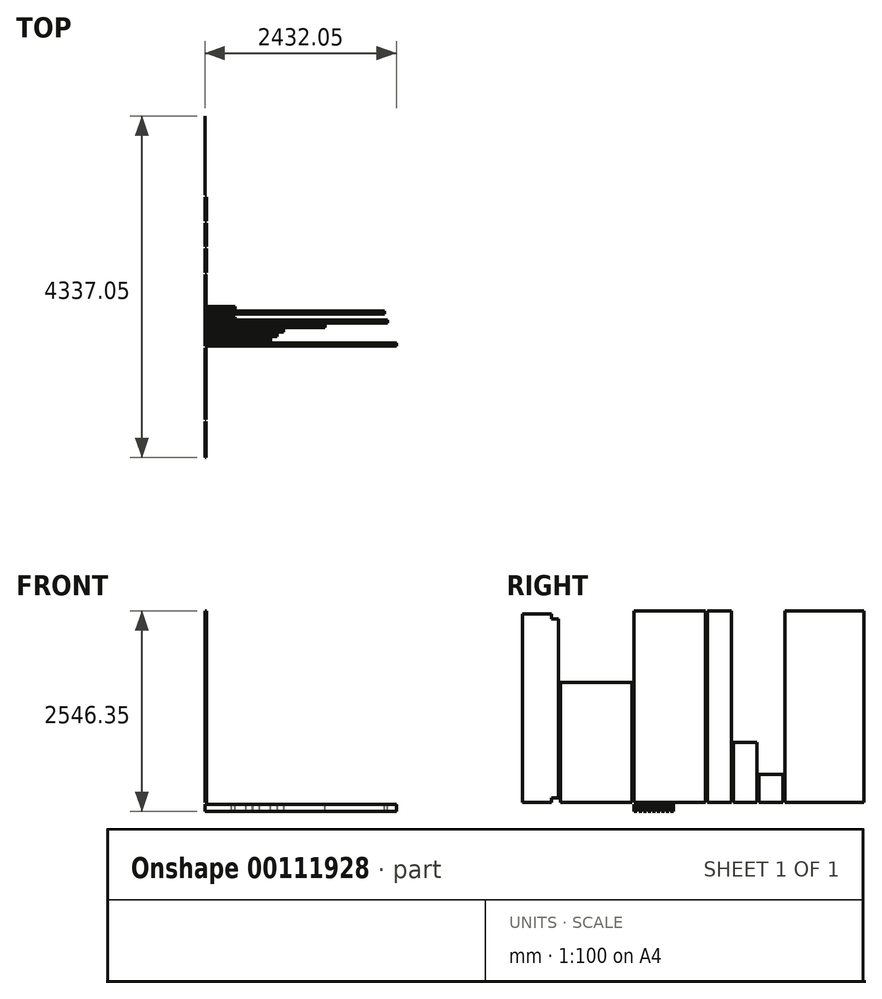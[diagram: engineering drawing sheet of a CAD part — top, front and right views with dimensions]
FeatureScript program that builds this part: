
annotation { "Feature Type Name" : "Feature", "Feature Type Description" : "" }
export const myFeature = defineFeature(function(context is Context, id is Id, definition is map)
    precondition{}
    {
        {
            var Q0;
            Q0=qCreatedBy(makeId("Right.planeOp"),FACE);
            var sketch = newSketch(context, id + "F0", { "sketchPlane" : qUnion([Q0])});
            skLineSegment(sketch, "E0.bottom", {"start": v(0, 0) * mm, "end": v(38.1, 0) * mm});
            skLineSegment(sketch, "E0.top", {"start": v(0, 88.9) * mm, "end": v(38.1, 88.9) * mm});
            skLineSegment(sketch, "E0.left", {"start": v(0, 0) * mm, "end": v(0, 88.9) * mm});
            skLineSegment(sketch, "E0.right", {"start": v(38.1, 0) * mm, "end": v(38.1, 88.9) * mm});
            skSolve(sketch);
        }
        {
            var Q0;
            Q0 = qSketchRegion(id + "F0", true);
            extrude(context, id + "F1", {"entities" : qUnion([Q0]), "depth" : 2432.05 * mm});
        }
        {
            var Q0;
            Q0=qCreatedBy(makeId("Right.planeOp"),FACE);
            var sketch = newSketch(context, id + "F2", { "sketchPlane" : qUnion([Q0])});
            skLineSegment(sketch, "E1.bottom", {"start": v(63.5, 0) * mm, "end": v(101.6, 0) * mm});
            skLineSegment(sketch, "E1.top", {"start": v(63.5, 88.9) * mm, "end": v(101.6, 88.9) * mm});
            skLineSegment(sketch, "E1.left", {"start": v(63.5, 0) * mm, "end": v(63.5, 88.9) * mm});
            skLineSegment(sketch, "E1.right", {"start": v(101.6, 0) * mm, "end": v(101.6, 88.9) * mm});
            skSolve(sketch);
        }
        {
            var Q0;
            Q0 = qSketchRegion(id + "F2", true);
            extrude(context, id + "F3", {"entities" : qUnion([Q0]), "depth" : 831.85 * mm});
        }
        {
            var Q0;
            Q0=qCreatedBy(makeId("Right.planeOp"),FACE);
            var sketch = newSketch(context, id + "F4", { "sketchPlane" : qUnion([Q0])});
            skLineSegment(sketch, "E2.bottom", {"start": v(120.65, 88.9) * mm, "end": v(158.75, 88.9) * mm});
            skLineSegment(sketch, "E2.top", {"start": v(120.65, 0) * mm, "end": v(158.75, 0) * mm});
            skLineSegment(sketch, "E2.left", {"start": v(120.65, 88.9) * mm, "end": v(120.65, 0) * mm});
            skLineSegment(sketch, "E2.right", {"start": v(158.75, 88.9) * mm, "end": v(158.75, 0) * mm});
            skLineSegment(sketch, "E3.bottom", {"start": v(177.8, 88.9) * mm, "end": v(215.9, 88.9) * mm});
            skLineSegment(sketch, "E3.top", {"start": v(177.8, 0) * mm, "end": v(215.9, 0) * mm});
            skLineSegment(sketch, "E3.left", {"start": v(177.8, 88.9) * mm, "end": v(177.8, 0) * mm});
            skLineSegment(sketch, "E3.right", {"start": v(215.9, 88.9) * mm, "end": v(215.9, 0) * mm});
            skLineSegment(sketch, "E4.bottom", {"start": v(0, 114.3) * mm, "end": v(908.05, 114.3) * mm});
            skLineSegment(sketch, "E4.top", {"start": v(0, 2546.35) * mm, "end": v(908.05, 2546.35) * mm});
            skLineSegment(sketch, "E4.left", {"start": v(0, 114.3) * mm, "end": v(0, 2546.35) * mm});
            skLineSegment(sketch, "E4.right", {"start": v(908.05, 114.3) * mm, "end": v(908.05, 2546.35) * mm});
            skLineSegment(sketch, "E5.bottom", {"start": v(933.45, 2546.35) * mm, "end": v(1238.25, 2546.35) * mm});
            skLineSegment(sketch, "E5.top", {"start": v(933.45, 114.3) * mm, "end": v(1238.25, 114.3) * mm});
            skLineSegment(sketch, "E5.left", {"start": v(933.45, 2546.35) * mm, "end": v(933.45, 114.3) * mm});
            skLineSegment(sketch, "E5.right", {"start": v(1238.25, 2546.35) * mm, "end": v(1238.25, 114.3) * mm});
            skLineSegment(sketch, "E6.bottom", {"start": v(1263.65, 876.3) * mm, "end": v(1562.1, 876.3) * mm});
            skLineSegment(sketch, "E6.top", {"start": v(1263.65, 114.3) * mm, "end": v(1562.1, 114.3) * mm});
            skLineSegment(sketch, "E6.left", {"start": v(1263.65, 876.3) * mm, "end": v(1263.65, 114.3) * mm});
            skLineSegment(sketch, "E6.right", {"start": v(1562.1, 876.3) * mm, "end": v(1562.1, 114.3) * mm});
            skLineSegment(sketch, "E7.bottom", {"start": v(1587.5, 114.3) * mm, "end": v(1892.3, 114.3) * mm});
            skLineSegment(sketch, "E7.top", {"start": v(1587.5, 469.9) * mm, "end": v(1892.3, 469.9) * mm});
            skLineSegment(sketch, "E7.left", {"start": v(1587.5, 114.3) * mm, "end": v(1587.5, 469.9) * mm});
            skLineSegment(sketch, "E7.right", {"start": v(1892.3, 114.3) * mm, "end": v(1892.3, 469.9) * mm});
            skLineSegment(sketch, "E8.bottom", {"start": v(234.95, 0) * mm, "end": v(273.05, 0) * mm});
            skLineSegment(sketch, "E8.top", {"start": v(234.95, 88.9) * mm, "end": v(273.05, 88.9) * mm});
            skLineSegment(sketch, "E8.left", {"start": v(234.95, 0) * mm, "end": v(234.95, 88.9) * mm});
            skLineSegment(sketch, "E8.right", {"start": v(273.05, 0) * mm, "end": v(273.05, 88.9) * mm});
            skLineSegment(sketch, "E9.bottom", {"start": v(-25.4, 114.3) * mm, "end": v(-933.45, 114.3) * mm});
            skLineSegment(sketch, "E9.top", {"start": v(-25.4, 1638.3) * mm, "end": v(-933.45, 1638.3) * mm});
            skLineSegment(sketch, "E9.left", {"start": v(-25.4, 114.3) * mm, "end": v(-25.4, 1638.3) * mm});
            skLineSegment(sketch, "E9.right", {"start": v(-933.45, 114.3) * mm, "end": v(-933.45, 1638.3) * mm});
            skLineSegment(sketch, "E10.bottom", {"start": v(292.1, 0) * mm, "end": v(330.2, 0) * mm});
            skLineSegment(sketch, "E10.top", {"start": v(292.1, 88.9) * mm, "end": v(330.2, 88.9) * mm});
            skLineSegment(sketch, "E10.left", {"start": v(292.1, 0) * mm, "end": v(292.1, 88.9) * mm});
            skLineSegment(sketch, "E10.right", {"start": v(330.2, 0) * mm, "end": v(330.2, 88.9) * mm});
            skLineSegment(sketch, "E11.bottom", {"start": v(349.25, 0) * mm, "end": v(387.35, 0) * mm});
            skLineSegment(sketch, "E11.top", {"start": v(349.25, 88.9) * mm, "end": v(387.35, 88.9) * mm});
            skLineSegment(sketch, "E11.left", {"start": v(349.25, 0) * mm, "end": v(349.25, 88.9) * mm});
            skLineSegment(sketch, "E11.right", {"start": v(387.35, 0) * mm, "end": v(387.35, 88.9) * mm});
            skLineSegment(sketch, "E12.bottom", {"start": v(406.4, 0) * mm, "end": v(444.5, 0) * mm});
            skLineSegment(sketch, "E12.top", {"start": v(406.4, 88.9) * mm, "end": v(444.5, 88.9) * mm});
            skLineSegment(sketch, "E12.left", {"start": v(406.4, 0) * mm, "end": v(406.4, 88.9) * mm});
            skLineSegment(sketch, "E12.right", {"start": v(444.5, 0) * mm, "end": v(444.5, 88.9) * mm});
            skLineSegment(sketch, "E13.bottom", {"start": v(463.55, 0) * mm, "end": v(501.65, 0) * mm});
            skLineSegment(sketch, "E13.top", {"start": v(463.55, 88.9) * mm, "end": v(501.65, 88.9) * mm});
            skLineSegment(sketch, "E13.left", {"start": v(463.55, 0) * mm, "end": v(463.55, 88.9) * mm});
            skLineSegment(sketch, "E13.right", {"start": v(501.65, 0) * mm, "end": v(501.65, 88.9) * mm});
            skLineSegment(sketch, "E14.bottom", {"start": v(-1047.75, 114.3) * mm, "end": v(-1416.05, 114.3) * mm});
            skLineSegment(sketch, "E14.top", {"start": v(-1047.75, 2508.25) * mm, "end": v(-1416.05, 2508.25) * mm});
            skLineSegment(sketch, "E14.left", {"start": v(-958.85, 174.63) * mm, "end": v(-958.85, 2447.93) * mm});
            skLineSegment(sketch, "E14.right", {"start": v(-1416.05, 114.3) * mm, "end": v(-1416.05, 2508.25) * mm});
            skLineSegment(sketch, "E15", {"start": v(-1047.75, 114.3) * mm, "end": v(-1047.75, 174.62) * mm});
            skLineSegment(sketch, "E16", {"start": v(-1047.75, 174.63) * mm, "end": v(-958.85, 174.63) * mm});
            skLineSegment(sketch, "E17", {"start": v(-1047.75, 2508.25) * mm, "end": v(-1047.75, 2447.93) * mm});
            skLineSegment(sketch, "E18", {"start": v(-1047.75, 2447.93) * mm, "end": v(-958.85, 2447.93) * mm});
            skLineSegment(sketch, "E19.bottom", {"start": v(1917.7, 114.3) * mm, "end": v(2921, 114.3) * mm});
            skLineSegment(sketch, "E19.top", {"start": v(1917.7, 2546.35) * mm, "end": v(2921, 2546.35) * mm});
            skLineSegment(sketch, "E19.left", {"start": v(1917.7, 114.3) * mm, "end": v(1917.7, 2546.35) * mm});
            skLineSegment(sketch, "E19.right", {"start": v(2921, 114.3) * mm, "end": v(2921, 2546.35) * mm});
            skSolve(sketch);
        }
        {
            var Q0;
            Q0=makeQuery(id+"F4.imprint","IMPRINT",FACE,{"disambiguationData":[TD([[makeQuery(id+"F4.imprint","IMPRINT",EDGE,{"derivedFrom":sQuery(id+"F4.wireOp",EDGE,"E2.bottom")}),-1.0]])]});
            extrude(context, id + "F5", {"entities" : qUnion([Q0]), "depth" : 914.4 * mm});
        }
        {
            var Q0;
            Q0=makeQuery(id+"F4.imprint","IMPRINT",FACE,{"disambiguationData":[TD([[makeQuery(id+"F4.imprint","IMPRINT",EDGE,{"derivedFrom":sQuery(id+"F4.wireOp",EDGE,"E3.bottom")}),-1.0]])]});
            extrude(context, id + "F6", {"entities" : qUnion([Q0]), "depth" : 1000.12 * mm});
        }
        {
            var Q0;
            Q0=makeQuery(id+"F6.opExtrude","SWEPT_FACE",FACE,{"disambiguationData":[OSD([sQuery(id+"F4.wireOp",EDGE,"E3.bottom")])]});
            var sketch = newSketch(context, id + "F7", { "sketchPlane" : qUnion([Q0])});
            skLineSegment(sketch, "E20.bottom", {"start": v(695.33, 177.8) * mm, "end": v(606.43, 177.8) * mm});
            skLineSegment(sketch, "E20.top", {"start": v(695.33, 196.85) * mm, "end": v(606.43, 196.85) * mm});
            skLineSegment(sketch, "E20.left", {"start": v(695.33, 177.8) * mm, "end": v(695.33, 196.85) * mm});
            skLineSegment(sketch, "E20.right", {"start": v(606.43, 177.8) * mm, "end": v(606.43, 196.85) * mm});
            skSolve(sketch);
        }
        {
            var Q0;
            Q0 = qSketchRegion(id + "F7", true);
            extrude(context, id + "F8", {"entities" : qUnion([Q0]), "operationType" : NewBodyOperationType.REMOVE, "endBound" : BoundingType.UP_TO_NEXT, "oppositeDirection" : true, "depth" : 25.4 * mm});
        }
        {
            var Q0;
            Q0=makeQuery(id+"F5.opExtrude","SWEPT_FACE",FACE,{"disambiguationData":[OSD([sQuery(id+"F4.wireOp",EDGE,"E2.bottom")])]});
            var sketch = newSketch(context, id + "F9", { "sketchPlane" : qUnion([Q0])});
            skLineSegment(sketch, "E21.bottom", {"start": v(609.6, 158.75) * mm, "end": v(520.7, 158.75) * mm});
            skLineSegment(sketch, "E21.top", {"start": v(609.6, 139.7) * mm, "end": v(520.7, 139.7) * mm});
            skLineSegment(sketch, "E21.left", {"start": v(609.6, 158.75) * mm, "end": v(609.6, 139.7) * mm});
            skLineSegment(sketch, "E21.right", {"start": v(520.7, 158.75) * mm, "end": v(520.7, 139.7) * mm});
            skSolve(sketch);
        }
        {
            var Q0;
            Q0 = qSketchRegion(id + "F9", true);
            extrude(context, id + "F10", {"entities" : qUnion([Q0]), "operationType" : NewBodyOperationType.REMOVE, "endBound" : BoundingType.UP_TO_NEXT, "oppositeDirection" : true, "depth" : 25.4 * mm});
        }
        {
            var Q0;
            Q0=makeQuery(id+"F4.imprint","IMPRINT",FACE,{"disambiguationData":[TD([[makeQuery(id+"F4.imprint","IMPRINT",EDGE,{"derivedFrom":sQuery(id+"F4.wireOp",EDGE,"E4.bottom")}),1.0]])]});
            var Q1;
            Q1=makeQuery(id+"F4.imprint","IMPRINT",FACE,{"disambiguationData":[TD([[makeQuery(id+"F4.imprint","IMPRINT",EDGE,{"derivedFrom":sQuery(id+"F4.wireOp",EDGE,"E9.bottom")}),-1.0]])]});
            var Q2;
            Q2=makeQuery(id+"F4.imprint","IMPRINT",FACE,{"disambiguationData":[TD([[makeQuery(id+"F4.imprint","IMPRINT",EDGE,{"derivedFrom":sQuery(id+"F4.wireOp",EDGE,"E14.bottom")}),-1.0]])]});
            extrude(context, id + "F11", {"entities" : qUnion([Q0, Q1, Q2]), "depth" : 12.7 * mm});
        }
        {
            var Q0;
            Q0=makeQuery(id+"F4.imprint","IMPRINT",FACE,{"disambiguationData":[TD([[makeQuery(id+"F4.imprint","IMPRINT",EDGE,{"derivedFrom":sQuery(id+"F4.wireOp",EDGE,"E5.bottom")}),-1.0]])]});
            var Q1;
            Q1=makeQuery(id+"F4.imprint","IMPRINT",FACE,{"disambiguationData":[TD([[makeQuery(id+"F4.imprint","IMPRINT",EDGE,{"derivedFrom":sQuery(id+"F4.wireOp",EDGE,"E6.bottom")}),-1.0]])]});
            var Q2;
            Q2=makeQuery(id+"F4.imprint","IMPRINT",FACE,{"disambiguationData":[TD([[makeQuery(id+"F4.imprint","IMPRINT",EDGE,{"derivedFrom":sQuery(id+"F4.wireOp",EDGE,"E7.bottom")}),1.0]])]});
            extrude(context, id + "F12", {"entities" : qUnion([Q0, Q1, Q2]), "depth" : 19.05 * mm});
        }
        {
            var Q0;
            Q0=makeQuery(id+"F4.imprint","IMPRINT",FACE,{"disambiguationData":[TD([[makeQuery(id+"F4.imprint","IMPRINT",EDGE,{"derivedFrom":sQuery(id+"F4.wireOp",EDGE,"E8.bottom")}),1.0]])]});
            extrude(context, id + "F13", {"entities" : qUnion([Q0]), "depth" : 1524 * mm});
        }
        {
            var Q0;
            Q0=makeQuery(id+"F4.imprint","IMPRINT",FACE,{"disambiguationData":[TD([[makeQuery(id+"F4.imprint","IMPRINT",EDGE,{"derivedFrom":sQuery(id+"F4.wireOp",EDGE,"E10.bottom")}),1.0]])]});
            extrude(context, id + "F14", {"entities" : qUnion([Q0]), "depth" : 2317.75 * mm});
        }
        {
            var Q0;
            Q0=makeQuery(id+"F4.imprint","IMPRINT",FACE,{"disambiguationData":[TD([[makeQuery(id+"F4.imprint","IMPRINT",EDGE,{"derivedFrom":sQuery(id+"F4.wireOp",EDGE,"E11.bottom")}),1.0]])]});
            var Q1;
            Q1=makeQuery(id+"F4.imprint","IMPRINT",FACE,{"disambiguationData":[TD([[makeQuery(id+"F4.imprint","IMPRINT",EDGE,{"derivedFrom":sQuery(id+"F4.wireOp",EDGE,"E13.bottom")}),1.0]])]});
            extrude(context, id + "F15", {"entities" : qUnion([Q0, Q1]), "depth" : 381 * mm});
        }
        {
            var Q0;
            Q0=makeQuery(id+"F4.imprint","IMPRINT",FACE,{"disambiguationData":[TD([[makeQuery(id+"F4.imprint","IMPRINT",EDGE,{"derivedFrom":sQuery(id+"F4.wireOp",EDGE,"E12.bottom")}),1.0]])]});
            extrude(context, id + "F16", {"entities" : qUnion([Q0]), "depth" : 2279.65 * mm});
        }
        {
            var Q0;
            Q0=makeQuery(id+"F15.opExtrude","SWEPT_FACE",FACE,{"disambiguationData":[OSD([sQuery(id+"F4.wireOp",EDGE,"E11.bottom")])]});
            var sketch = newSketch(context, id + "F17", { "sketchPlane" : qUnion([Q0])});
            skPoint(sketch, "E22.oppositeSnap0", {"position": v(381, -368.3) * mm});
            skLineSegment(sketch, "E22.bottom", {"start": v(381, -387.35) * mm, "end": v(330.2, -387.35) * mm});
            skLineSegment(sketch, "E22.top", {"start": v(381, -368.3) * mm, "end": v(330.2, -368.3) * mm});
            skLineSegment(sketch, "E22.left", {"start": v(381, -387.35) * mm, "end": v(381, -368.3) * mm});
            skLineSegment(sketch, "E22.right", {"start": v(330.2, -387.35) * mm, "end": v(330.2, -368.3) * mm});
            skSolve(sketch);
        }
        {
            var Q0;
            Q0=makeQuery(id+"F17.imprint","IMPRINT",FACE,{"disambiguationData":[TD([[makeQuery(id+"F17.imprint","IMPRINT",EDGE,{"derivedFrom":sQuery(id+"F17.wireOp",EDGE,"E22.bottom")}),-1.0]])]});
            extrude(context, id + "F18", {"entities" : qUnion([Q0]), "operationType" : NewBodyOperationType.REMOVE, "endBound" : BoundingType.UP_TO_NEXT, "oppositeDirection" : true, "depth" : 25.4 * mm});
        }
        {
            var Q0;
            Q0=makeQuery(id+"F4.imprint","IMPRINT",FACE,{"disambiguationData":[TD([[makeQuery(id+"F4.imprint","IMPRINT",EDGE,{"derivedFrom":sQuery(id+"F4.wireOp",EDGE,"E19.bottom")}),1.0]])]});
            extrude(context, id + "F19", {"entities" : qUnion([Q0]), "depth" : 3.17 * mm});
        }
    });
